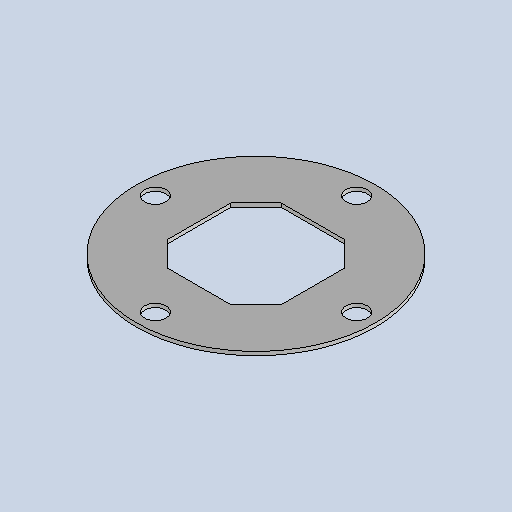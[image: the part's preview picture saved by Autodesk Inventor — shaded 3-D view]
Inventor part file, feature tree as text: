
AUTODESK INVENTOR PART (.ipt)
format: ipt  version: 2025.1 (Build 291241020, 241B)  size: 171,520 bytes
history: native  units: mm
features: other x4, sketch x2, sheet_metal_op x1, pattern_circular x1
ambient origin geometry x8: Origin, YZ Plane, XZ Plane, XY Plane, X Axis, Y Axis, Z Axis, Center Point
bodies: Body1 (feature_tree)
feature tree (8):
  sheet_metal_op  "Face3"
  pattern_circular  "Circular Pattern1"  Count=50  [1 undecoded]
  other  "Corner Chamfer2"
  sketch  "Sketch1"  dims[d156=3.0mm]
  other  "Plate5"
  sketch  "Sketch7"  dims[d157=190.0mm d158=90.0mm d159=90.0mm d160=17.0mm d161=80.0mm d162=3.0mm d163=0.0mm d164=40.0mm d165=360.0deg d167=20.0mm d168=6.0mm d169=45.0deg]
  other  "Cut1"
  other  "Definition1"
note: 1 required parameter value undecoded (feature->parameter linkage not recoverable at this tier; creation-order binding heuristic only, values carry confidence <= 0.55)
